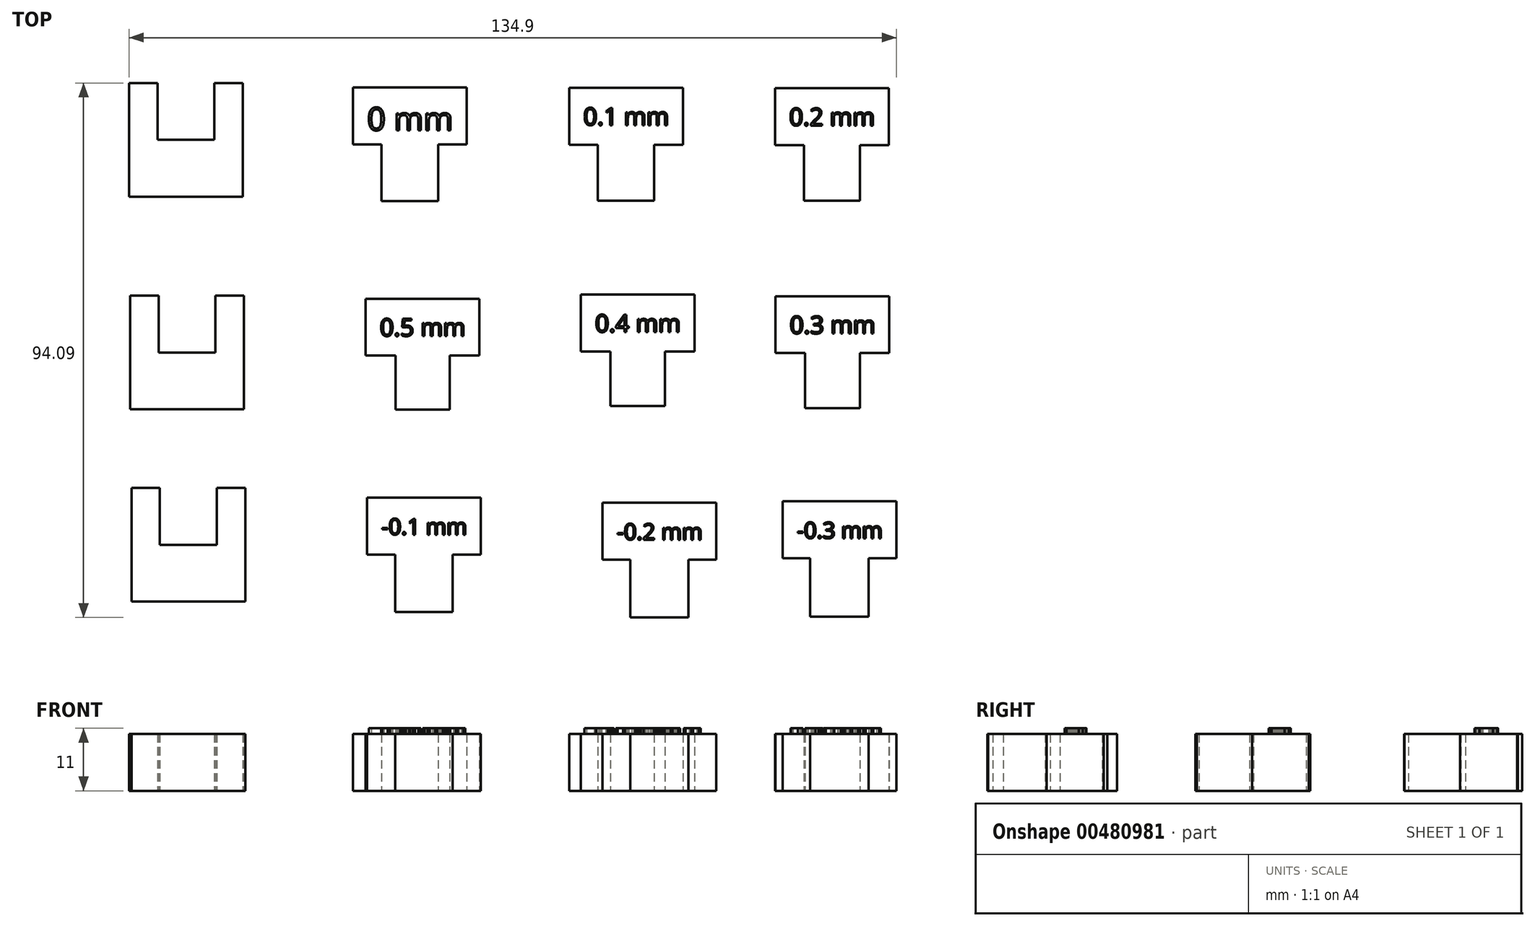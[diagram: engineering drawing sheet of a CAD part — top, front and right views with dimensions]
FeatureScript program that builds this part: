
annotation { "Feature Type Name" : "Feature", "Feature Type Description" : "" }
export const myFeature = defineFeature(function(context is Context, id is Id, definition is map)
    precondition{}
    {
        {
            var Q0;
            Q0=qCreatedBy(makeId("Top.planeOp"),FACE);
            var sketch = newSketch(context, id + "F0", { "sketchPlane" : qUnion([Q0])});
            skLineSegment(sketch, "E0", {"start": v(-61.95, 43.82) * mm, "end": v(-61.95, 23.82) * mm});
            skLineSegment(sketch, "E1", {"start": v(-61.95, 23.82) * mm, "end": v(-41.95, 23.82) * mm});
            skLineSegment(sketch, "E2", {"start": v(-41.95, 23.82) * mm, "end": v(-41.95, 43.82) * mm});
            skLineSegment(sketch, "E3", {"start": v(-41.95, 43.82) * mm, "end": v(-46.95, 43.82) * mm});
            skLineSegment(sketch, "E4", {"start": v(-46.95, 43.82) * mm, "end": v(-46.95, 33.82) * mm});
            skLineSegment(sketch, "E5", {"start": v(-46.95, 33.82) * mm, "end": v(-56.95, 33.82) * mm});
            skLineSegment(sketch, "E6", {"start": v(-56.95, 33.82) * mm, "end": v(-56.95, 43.82) * mm});
            skLineSegment(sketch, "E7", {"start": v(-56.95, 43.82) * mm, "end": v(-61.95, 43.82) * mm});
            skLineSegment(sketch, "E8", {"start": v(-17.58, 33.01) * mm, "end": v(-17.58, 23.01) * mm});
            skLineSegment(sketch, "E9", {"start": v(-17.58, 23.01) * mm, "end": v(-7.58, 23.01) * mm});
            skLineSegment(sketch, "E10", {"start": v(-7.58, 23.01) * mm, "end": v(-7.58, 33.01) * mm});
            skLineSegment(sketch, "E11", {"start": v(-7.58, 33.01) * mm, "end": v(-2.58, 33.01) * mm});
            skLineSegment(sketch, "E12", {"start": v(-2.58, 33.01) * mm, "end": v(-2.58, 43.01) * mm});
            skLineSegment(sketch, "E13", {"start": v(-2.58, 43.01) * mm, "end": v(-22.58, 43.01) * mm});
            skLineSegment(sketch, "E14", {"start": v(-22.58, 43.01) * mm, "end": v(-22.58, 33.01) * mm});
            skLineSegment(sketch, "E15", {"start": v(-22.58, 33.01) * mm, "end": v(-17.58, 33.01) * mm});
            skLineSegment(sketch, "E16", {"start": v(20.48, 32.96) * mm, "end": v(20.48, 23.06) * mm});
            skLineSegment(sketch, "E17", {"start": v(20.48, 23.06) * mm, "end": v(30.38, 23.06) * mm});
            skLineSegment(sketch, "E18", {"start": v(30.38, 23.06) * mm, "end": v(30.38, 32.96) * mm});
            skLineSegment(sketch, "E19", {"start": v(30.38, 32.96) * mm, "end": v(35.43, 32.96) * mm});
            skLineSegment(sketch, "E20", {"start": v(35.43, 32.96) * mm, "end": v(35.43, 42.96) * mm});
            skLineSegment(sketch, "E21", {"start": v(35.43, 42.96) * mm, "end": v(15.43, 42.96) * mm});
            skLineSegment(sketch, "E22", {"start": v(15.43, 42.96) * mm, "end": v(15.43, 32.96) * mm});
            skLineSegment(sketch, "E23", {"start": v(15.43, 32.96) * mm, "end": v(20.48, 32.96) * mm});
            skLineSegment(sketch, "E24", {"start": v(56.73, 32.9) * mm, "end": v(56.73, 23.1) * mm});
            skLineSegment(sketch, "E25", {"start": v(56.73, 23.1) * mm, "end": v(66.53, 23.1) * mm});
            skLineSegment(sketch, "E26", {"start": v(66.53, 23.1) * mm, "end": v(66.53, 32.9) * mm});
            skLineSegment(sketch, "E27", {"start": v(66.53, 32.9) * mm, "end": v(71.63, 32.9) * mm});
            skLineSegment(sketch, "E28", {"start": v(71.63, 32.9) * mm, "end": v(71.63, 42.9) * mm});
            skLineSegment(sketch, "E29", {"start": v(71.63, 42.9) * mm, "end": v(51.63, 42.9) * mm});
            skLineSegment(sketch, "E30", {"start": v(51.63, 42.9) * mm, "end": v(51.63, 32.9) * mm});
            skLineSegment(sketch, "E31", {"start": v(51.63, 32.9) * mm, "end": v(56.73, 32.9) * mm});
            skLineSegment(sketch, "E32", {"start": v(56.88, -3.71) * mm, "end": v(56.88, -13.41) * mm});
            skLineSegment(sketch, "E33", {"start": v(56.88, -13.41) * mm, "end": v(66.58, -13.41) * mm});
            skLineSegment(sketch, "E34", {"start": v(66.58, -13.41) * mm, "end": v(66.58, -3.71) * mm});
            skLineSegment(sketch, "E35", {"start": v(66.58, -3.71) * mm, "end": v(71.73, -3.71) * mm});
            skLineSegment(sketch, "E36", {"start": v(71.73, -3.71) * mm, "end": v(71.73, 6.29) * mm});
            skLineSegment(sketch, "E37", {"start": v(71.73, 6.29) * mm, "end": v(51.73, 6.29) * mm});
            skLineSegment(sketch, "E38", {"start": v(51.73, 6.29) * mm, "end": v(51.73, -3.71) * mm});
            skLineSegment(sketch, "E39", {"start": v(51.73, -3.71) * mm, "end": v(56.88, -3.71) * mm});
            skLineSegment(sketch, "E40", {"start": v(22.7, -3.44) * mm, "end": v(22.7, -13.04) * mm});
            skLineSegment(sketch, "E41", {"start": v(22.7, -13.04) * mm, "end": v(32.3, -13.04) * mm});
            skLineSegment(sketch, "E42", {"start": v(32.3, -13.04) * mm, "end": v(32.3, -3.44) * mm});
            skLineSegment(sketch, "E43", {"start": v(32.3, -3.44) * mm, "end": v(37.5, -3.44) * mm});
            skLineSegment(sketch, "E44", {"start": v(37.5, -3.44) * mm, "end": v(37.5, 6.56) * mm});
            skLineSegment(sketch, "E45", {"start": v(37.5, 6.56) * mm, "end": v(17.5, 6.56) * mm});
            skLineSegment(sketch, "E46", {"start": v(17.5, 6.56) * mm, "end": v(17.5, -3.44) * mm});
            skLineSegment(sketch, "E47", {"start": v(17.5, -3.44) * mm, "end": v(22.7, -3.44) * mm});
            skLineSegment(sketch, "E48", {"start": v(-15.1, -4.16) * mm, "end": v(-15.1, -13.66) * mm});
            skLineSegment(sketch, "E49", {"start": v(-15.1, -13.66) * mm, "end": v(-5.6, -13.66) * mm});
            skLineSegment(sketch, "E50", {"start": v(-5.6, -13.66) * mm, "end": v(-5.6, -4.16) * mm});
            skLineSegment(sketch, "E51", {"start": v(-5.6, -4.16) * mm, "end": v(-0.35, -4.16) * mm});
            skLineSegment(sketch, "E52", {"start": v(-0.35, -4.16) * mm, "end": v(-0.35, 5.84) * mm});
            skLineSegment(sketch, "E53", {"start": v(-0.35, 5.84) * mm, "end": v(-20.35, 5.84) * mm});
            skLineSegment(sketch, "E54", {"start": v(-20.35, 5.84) * mm, "end": v(-20.35, -4.16) * mm});
            skLineSegment(sketch, "E55", {"start": v(-20.35, -4.16) * mm, "end": v(-15.1, -4.16) * mm});
            skLineSegment(sketch, "E56", {"start": v(-15.16, -39.18) * mm, "end": v(-15.16, -49.28) * mm});
            skLineSegment(sketch, "E57", {"start": v(-15.16, -49.28) * mm, "end": v(-5.06, -49.28) * mm});
            skLineSegment(sketch, "E58", {"start": v(-5.06, -49.28) * mm, "end": v(-5.06, -39.18) * mm});
            skLineSegment(sketch, "E59", {"start": v(-5.06, -39.18) * mm, "end": v(-0.1, -39.18) * mm});
            skLineSegment(sketch, "E60", {"start": v(-0.1, -39.18) * mm, "end": v(-0.1, -29.18) * mm});
            skLineSegment(sketch, "E61", {"start": v(-0.1, -29.18) * mm, "end": v(-20.1, -29.18) * mm});
            skLineSegment(sketch, "E62", {"start": v(-20.1, -29.18) * mm, "end": v(-20.1, -39.18) * mm});
            skLineSegment(sketch, "E63", {"start": v(-20.1, -39.18) * mm, "end": v(-15.16, -39.18) * mm});
            skLineSegment(sketch, "E64", {"start": v(26.19, -40.07) * mm, "end": v(26.19, -50.27) * mm});
            skLineSegment(sketch, "E65", {"start": v(26.19, -50.27) * mm, "end": v(36.39, -50.27) * mm});
            skLineSegment(sketch, "E66", {"start": v(36.39, -50.27) * mm, "end": v(36.39, -40.07) * mm});
            skLineSegment(sketch, "E67", {"start": v(36.39, -40.07) * mm, "end": v(41.29, -40.07) * mm});
            skLineSegment(sketch, "E68", {"start": v(41.29, -40.07) * mm, "end": v(41.29, -30.07) * mm});
            skLineSegment(sketch, "E69", {"start": v(41.29, -30.07) * mm, "end": v(21.29, -30.07) * mm});
            skLineSegment(sketch, "E70", {"start": v(21.29, -30.07) * mm, "end": v(21.29, -40.07) * mm});
            skLineSegment(sketch, "E71", {"start": v(21.29, -40.07) * mm, "end": v(26.19, -40.07) * mm});
            skLineSegment(sketch, "E72", {"start": v(57.8, -39.82) * mm, "end": v(57.8, -50.12) * mm});
            skLineSegment(sketch, "E73", {"start": v(57.8, -50.12) * mm, "end": v(68.1, -50.12) * mm});
            skLineSegment(sketch, "E74", {"start": v(68.1, -50.12) * mm, "end": v(68.1, -39.82) * mm});
            skLineSegment(sketch, "E75", {"start": v(68.1, -39.82) * mm, "end": v(72.95, -39.82) * mm});
            skLineSegment(sketch, "E76", {"start": v(72.95, -39.82) * mm, "end": v(72.95, -29.82) * mm});
            skLineSegment(sketch, "E77", {"start": v(72.95, -29.82) * mm, "end": v(52.95, -29.82) * mm});
            skLineSegment(sketch, "E78", {"start": v(52.95, -29.82) * mm, "end": v(52.95, -39.82) * mm});
            skLineSegment(sketch, "E79", {"start": v(52.95, -39.82) * mm, "end": v(57.8, -39.82) * mm});
            skLineSegment(sketch, "E80", {"start": v(-61.75, 6.39) * mm, "end": v(-61.75, -13.61) * mm});
            skLineSegment(sketch, "E81", {"start": v(-61.75, -13.61) * mm, "end": v(-41.75, -13.61) * mm});
            skLineSegment(sketch, "E82", {"start": v(-41.75, -13.61) * mm, "end": v(-41.75, 6.39) * mm});
            skLineSegment(sketch, "E83", {"start": v(-41.75, 6.39) * mm, "end": v(-46.75, 6.39) * mm});
            skLineSegment(sketch, "E84", {"start": v(-46.75, 6.39) * mm, "end": v(-46.75, -3.61) * mm});
            skLineSegment(sketch, "E85", {"start": v(-46.75, -3.61) * mm, "end": v(-56.75, -3.61) * mm});
            skLineSegment(sketch, "E86", {"start": v(-56.75, -3.61) * mm, "end": v(-56.75, 6.39) * mm});
            skLineSegment(sketch, "E87", {"start": v(-56.75, 6.39) * mm, "end": v(-61.75, 6.39) * mm});
            skLineSegment(sketch, "E88", {"start": v(-61.54, -27.48) * mm, "end": v(-61.54, -47.48) * mm});
            skLineSegment(sketch, "E89", {"start": v(-61.54, -47.48) * mm, "end": v(-41.54, -47.48) * mm});
            skLineSegment(sketch, "E90", {"start": v(-41.54, -47.48) * mm, "end": v(-41.54, -27.48) * mm});
            skLineSegment(sketch, "E91", {"start": v(-41.54, -27.48) * mm, "end": v(-46.54, -27.48) * mm});
            skLineSegment(sketch, "E92", {"start": v(-46.54, -27.48) * mm, "end": v(-46.54, -37.48) * mm});
            skLineSegment(sketch, "E93", {"start": v(-46.54, -37.48) * mm, "end": v(-56.54, -37.48) * mm});
            skLineSegment(sketch, "E94", {"start": v(-56.54, -37.48) * mm, "end": v(-56.54, -27.48) * mm});
            skLineSegment(sketch, "E95", {"start": v(-56.54, -27.48) * mm, "end": v(-61.54, -27.48) * mm});
            skSolve(sketch);
        }
        {
            var Q0;
            Q0=qSketchRegion(id+"F0",true);
            extrude(context, id + "F1", {"entities" : qUnion([Q0]), "depth" : 10 * mm});
        }
        {
            var Q0;
            Q0=makeQuery(id+"F1.opExtrude","CAP_FACE",FACE,{"disambiguationData":[OSD([sQuery(id+"F0.wireOp",EDGE,"E8"),sQuery(id+"F0.wireOp",EDGE,"E9"),sQuery(id+"F0.wireOp",EDGE,"E10"),sQuery(id+"F0.wireOp",EDGE,"E11"),sQuery(id+"F0.wireOp",EDGE,"E12"),sQuery(id+"F0.wireOp",EDGE,"E13"),sQuery(id+"F0.wireOp",EDGE,"E14"),sQuery(id+"F0.wireOp",EDGE,"E15")])],"isStart":false});
            var sketch = newSketch(context, id + "F2", { "sketchPlane" : qUnion([Q0])});
            skText(sketch, "E96", { "text": "0 mm", "fontName": "OpenSans-Regular.ttf"});
            const initialGuessF2  = {"E96": [-0.02008, 0.03548, 1, 0, 0.00404]};
            skSetInitialGuess(sketch, initialGuessF2);
            skSolve(sketch);
        }
        {
            var Q0;
            Q0=qSketchRegion(id+"F2",true);
            extrude(context, id + "F3", {"entities" : qUnion([Q0]), "operationType" : NewBodyOperationType.ADD, "depth" : 1 * mm});
        }
        {
            var Q0;
            Q0=makeQuery(id+"F1.opExtrude","CAP_FACE",FACE,{"disambiguationData":[OSD([sQuery(id+"F0.wireOp",EDGE,"E16"),sQuery(id+"F0.wireOp",EDGE,"E17"),sQuery(id+"F0.wireOp",EDGE,"E18"),sQuery(id+"F0.wireOp",EDGE,"E19"),sQuery(id+"F0.wireOp",EDGE,"E20"),sQuery(id+"F0.wireOp",EDGE,"E21"),sQuery(id+"F0.wireOp",EDGE,"E22"),sQuery(id+"F0.wireOp",EDGE,"E23")])],"isStart":false});
            var sketch = newSketch(context, id + "F4", { "sketchPlane" : qUnion([Q0])});
            skText(sketch, "E97", { "text": "0.1 mm", "fontName": "OpenSans-Regular.ttf"});
            const initialGuessF4  = {"E97": [0.01793, 0.03639, 1, 0, 0.00307]};
            skSetInitialGuess(sketch, initialGuessF4);
            skSolve(sketch);
        }
        {
            var Q0;
            Q0=qSketchRegion(id+"F4",true);
            extrude(context, id + "F5", {"entities" : qUnion([Q0]), "operationType" : NewBodyOperationType.ADD, "depth" : 1 * mm});
        }
        {
            var Q0;
            Q0=makeQuery(id+"F1.opExtrude","CAP_FACE",FACE,{"disambiguationData":[OSD([sQuery(id+"F0.wireOp",EDGE,"E24"),sQuery(id+"F0.wireOp",EDGE,"E25"),sQuery(id+"F0.wireOp",EDGE,"E26"),sQuery(id+"F0.wireOp",EDGE,"E27"),sQuery(id+"F0.wireOp",EDGE,"E28"),sQuery(id+"F0.wireOp",EDGE,"E29"),sQuery(id+"F0.wireOp",EDGE,"E30"),sQuery(id+"F0.wireOp",EDGE,"E31")])],"isStart":false});
            var sketch = newSketch(context, id + "F6", { "sketchPlane" : qUnion([Q0])});
            skText(sketch, "E98", { "text": "0.2 mm", "fontName": "OpenSans-Regular.ttf"});
            const initialGuessF6  = {"E98": [0.05413, 0.03632, 1, 0, 0.00307]};
            skSetInitialGuess(sketch, initialGuessF6);
            skSolve(sketch);
        }
        {
            var Q0;
            Q0=qSketchRegion(id+"F6",true);
            extrude(context, id + "F7", {"entities" : qUnion([Q0]), "operationType" : NewBodyOperationType.ADD, "depth" : 1 * mm});
        }
        {
            var Q0;
            Q0=makeQuery(id+"F1.opExtrude","CAP_FACE",FACE,{"disambiguationData":[OSD([sQuery(id+"F0.wireOp",EDGE,"E48"),sQuery(id+"F0.wireOp",EDGE,"E49"),sQuery(id+"F0.wireOp",EDGE,"E50"),sQuery(id+"F0.wireOp",EDGE,"E51"),sQuery(id+"F0.wireOp",EDGE,"E52"),sQuery(id+"F0.wireOp",EDGE,"E53"),sQuery(id+"F0.wireOp",EDGE,"E54"),sQuery(id+"F0.wireOp",EDGE,"E55")])],"isStart":false});
            var sketch = newSketch(context, id + "F8", { "sketchPlane" : qUnion([Q0])});
            skText(sketch, "E99", { "text": "0.5 mm", "fontName": "OpenSans-Regular.ttf"});
            const initialGuessF8  = {"E99": [-0.01785, -0.00073, 1, 0, 0.00307]};
            skSetInitialGuess(sketch, initialGuessF8);
            skSolve(sketch);
        }
        {
            var Q0;
            Q0=qSketchRegion(id+"F8",true);
            extrude(context, id + "F9", {"entities" : qUnion([Q0]), "operationType" : NewBodyOperationType.ADD, "depth" : 1 * mm});
        }
        {
            var Q0;
            Q0=makeQuery(id+"F1.opExtrude","CAP_FACE",FACE,{"disambiguationData":[OSD([sQuery(id+"F0.wireOp",EDGE,"E40"),sQuery(id+"F0.wireOp",EDGE,"E41"),sQuery(id+"F0.wireOp",EDGE,"E42"),sQuery(id+"F0.wireOp",EDGE,"E43"),sQuery(id+"F0.wireOp",EDGE,"E44"),sQuery(id+"F0.wireOp",EDGE,"E45"),sQuery(id+"F0.wireOp",EDGE,"E46"),sQuery(id+"F0.wireOp",EDGE,"E47")])],"isStart":false});
            var sketch = newSketch(context, id + "F10", { "sketchPlane" : qUnion([Q0])});
            skText(sketch, "E100", { "text": "0.4 mm", "fontName": "OpenSans-Regular.ttf"});
            const initialGuessF10  = {"E100": [0.02, -2e-05, 1, 0, 0.00307]};
            skSetInitialGuess(sketch, initialGuessF10);
            skSolve(sketch);
        }
        {
            var Q0;
            Q0=qSketchRegion(id+"F10",true);
            extrude(context, id + "F11", {"entities" : qUnion([Q0]), "operationType" : NewBodyOperationType.ADD, "depth" : 1 * mm});
        }
        {
            var Q0;
            Q0=makeQuery(id+"F1.opExtrude","CAP_FACE",FACE,{"disambiguationData":[OSD([sQuery(id+"F0.wireOp",EDGE,"E32"),sQuery(id+"F0.wireOp",EDGE,"E33"),sQuery(id+"F0.wireOp",EDGE,"E34"),sQuery(id+"F0.wireOp",EDGE,"E35"),sQuery(id+"F0.wireOp",EDGE,"E36"),sQuery(id+"F0.wireOp",EDGE,"E37"),sQuery(id+"F0.wireOp",EDGE,"E38"),sQuery(id+"F0.wireOp",EDGE,"E39")])],"isStart":false});
            var sketch = newSketch(context, id + "F12", { "sketchPlane" : qUnion([Q0])});
            skText(sketch, "E101", { "text": "0.3 mm", "fontName": "OpenSans-Regular.ttf"});
            const initialGuessF12  = {"E101": [0.05423, -0.00029, 1, 0, 0.00307]};
            skSetInitialGuess(sketch, initialGuessF12);
            skSolve(sketch);
        }
        {
            var Q0;
            Q0=qSketchRegion(id+"F12",true);
            extrude(context, id + "F13", {"entities" : qUnion([Q0]), "operationType" : NewBodyOperationType.ADD, "depth" : 1 * mm});
        }
        {
            var Q0;
            Q0=makeQuery(id+"F1.opExtrude","CAP_FACE",FACE,{"disambiguationData":[OSD([sQuery(id+"F0.wireOp",EDGE,"E56"),sQuery(id+"F0.wireOp",EDGE,"E57"),sQuery(id+"F0.wireOp",EDGE,"E58"),sQuery(id+"F0.wireOp",EDGE,"E59"),sQuery(id+"F0.wireOp",EDGE,"E60"),sQuery(id+"F0.wireOp",EDGE,"E61"),sQuery(id+"F0.wireOp",EDGE,"E62"),sQuery(id+"F0.wireOp",EDGE,"E63")])],"isStart":false});
            var sketch = newSketch(context, id + "F14", { "sketchPlane" : qUnion([Q0])});
            skText(sketch, "E102", { "text": "-0.1 mm", "fontName": "OpenSans-Regular.ttf"});
            const initialGuessF14  = {"E102": [-0.0176, -0.03568, 1, 0, 0.00282]};
            skSetInitialGuess(sketch, initialGuessF14);
            skSolve(sketch);
        }
        {
            var Q0;
            Q0=qSketchRegion(id+"F14",true);
            extrude(context, id + "F15", {"entities" : qUnion([Q0]), "operationType" : NewBodyOperationType.ADD, "depth" : 1 * mm});
        }
        {
            var Q0;
            Q0=makeQuery(id+"F1.opExtrude","CAP_FACE",FACE,{"disambiguationData":[OSD([sQuery(id+"F0.wireOp",EDGE,"E64"),sQuery(id+"F0.wireOp",EDGE,"E65"),sQuery(id+"F0.wireOp",EDGE,"E66"),sQuery(id+"F0.wireOp",EDGE,"E67"),sQuery(id+"F0.wireOp",EDGE,"E68"),sQuery(id+"F0.wireOp",EDGE,"E69"),sQuery(id+"F0.wireOp",EDGE,"E70"),sQuery(id+"F0.wireOp",EDGE,"E71")])],"isStart":false});
            var sketch = newSketch(context, id + "F16", { "sketchPlane" : qUnion([Q0])});
            skText(sketch, "E103", { "text": "-0.2 mm", "fontName": "OpenSans-Regular.ttf"});
            const initialGuessF16  = {"E103": [0.02379, -0.03657, 1, 0, 0.00282]};
            skSetInitialGuess(sketch, initialGuessF16);
            skSolve(sketch);
        }
        {
            var Q0;
            Q0=qSketchRegion(id+"F16",true);
            extrude(context, id + "F17", {"entities" : qUnion([Q0]), "operationType" : NewBodyOperationType.ADD, "depth" : 1 * mm});
        }
        {
            var Q0;
            Q0=makeQuery(id+"F1.opExtrude","CAP_FACE",FACE,{"disambiguationData":[OSD([sQuery(id+"F0.wireOp",EDGE,"E72"),sQuery(id+"F0.wireOp",EDGE,"E73"),sQuery(id+"F0.wireOp",EDGE,"E74"),sQuery(id+"F0.wireOp",EDGE,"E75"),sQuery(id+"F0.wireOp",EDGE,"E76"),sQuery(id+"F0.wireOp",EDGE,"E77"),sQuery(id+"F0.wireOp",EDGE,"E78"),sQuery(id+"F0.wireOp",EDGE,"E79")])],"isStart":false});
            var sketch = newSketch(context, id + "F18", { "sketchPlane" : qUnion([Q0])});
            skText(sketch, "E104", { "text": "-0.3 mm", "fontName": "OpenSans-Regular.ttf"});
            const initialGuessF18  = {"E104": [0.05545, -0.03632, 1, 0, 0.00282]};
            skSetInitialGuess(sketch, initialGuessF18);
            skSolve(sketch);
        }
        {
            var Q0;
            Q0=qSketchRegion(id+"F18",true);
            extrude(context, id + "F19", {"entities" : qUnion([Q0]), "operationType" : NewBodyOperationType.ADD, "depth" : 1 * mm});
        }
    });
